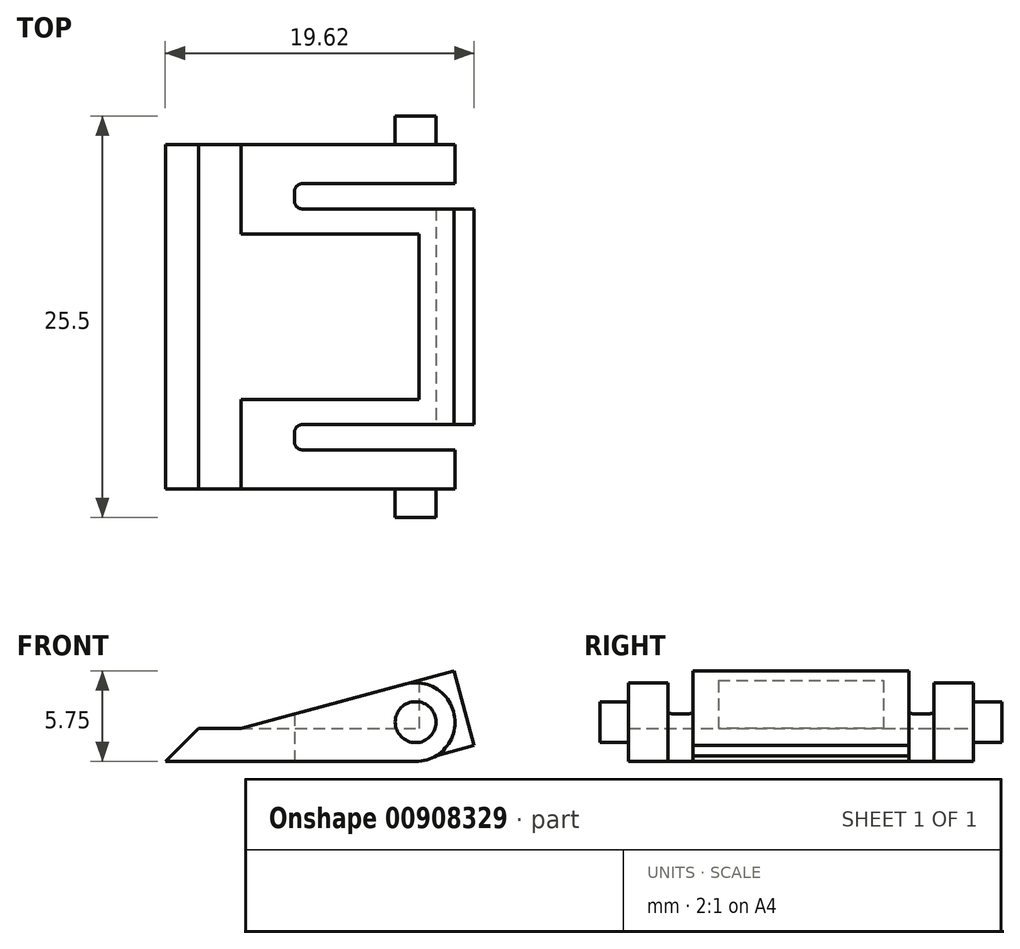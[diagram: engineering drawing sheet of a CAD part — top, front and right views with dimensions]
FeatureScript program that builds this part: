
annotation { "Feature Type Name" : "Feature", "Feature Type Description" : "" }
export const myFeature = defineFeature(function(context is Context, id is Id, definition is map)
    precondition{}
    {
        {
            var Q0;
            Q0=qCreatedBy(makeId("Front.planeOp"),FACE);
            var sketch = newSketch(context, id + "F0", { "sketchPlane" : qUnion([Q0])});
            skLineSegment(sketch, "E0", {"start": v(-10.84, 0) * mm, "end": v(5.06, 0) * mm});
            skArc(sketch, "E1", {"start": v(5.06, 0) * mm, "mid": v(7.54, 2.83) * mm, "end": v(4.41, 4.91) * mm});
            skLineSegment(sketch, "E2", {"start": v(-10.84, 0) * mm, "end": v(-8.74, 2.1) * mm});
            skLineSegment(sketch, "E3", {"start": v(-8.74, 2.1) * mm, "end": v(-6.04, 2.1) * mm});
            skLineSegment(sketch, "E4", {"start": v(-6.04, 2.1) * mm, "end": v(4.41, 4.91) * mm});
            skSolve(sketch);
        }
        {
            var Q0;
            Q0 = qSketchRegion(id + "F0", true);
            extrude(context, id + "F1", {"entities" : qUnion([Q0]), "endBound" : BoundingType.SYMMETRIC, "depth" : 21.9 * mm, "offsetDistance" : 25 * mm});
        }
        {
            var Q0;
            Q0=makeQuery(id+"F1.opExtrude","CAP_FACE",FACE,{"disambiguationData":[OSD([sQuery(id+"F0.wireOp",EDGE,"E0"),sQuery(id+"F0.wireOp",EDGE,"E1"),sQuery(id+"F0.wireOp",EDGE,"E2"),sQuery(id+"F0.wireOp",EDGE,"E3"),sQuery(id+"F0.wireOp",EDGE,"E4")])],"isStart":false});
            var sketch = newSketch(context, id + "F2", { "sketchPlane" : qUnion([Q0])});
            skPoint(sketch, "E5.0", {"position": v(5.06, 2.5) * mm});
            skCircle(sketch, "E6", {"center": v(5.06, 2.5) * mm, "radius": 1.3 * mm});
            skSolve(sketch);
        }
        {
            var Q0;
            Q0 = qSketchRegion(id + "F2", true);
            extrude(context, id + "F3", {"entities" : qUnion([Q0]), "operationType" : NewBodyOperationType.ADD, "depth" : 1.8 * mm, "offsetDistance" : 25 * mm});
        }
        {
            var Q0;
            Q0=makeQuery(id+"F1.opExtrude","SWEPT_BODY",BODY,{"disambiguationData":[OSD([sQuery(id+"F0.wireOp",EDGE,"E0"),sQuery(id+"F0.wireOp",EDGE,"E1"),sQuery(id+"F0.wireOp",EDGE,"E2"),sQuery(id+"F0.wireOp",EDGE,"E3"),sQuery(id+"F0.wireOp",EDGE,"E4")])]});
            var Q1;
            Q1=qCreatedBy(makeId("Front.planeOp"),FACE);
            mirror(context, id + "F4", {"operationType" : NewBodyOperationType.ADD, "entities" : qUnion([Q0]), "mirrorPlane" : qUnion([Q1])});
        }
        {
            var Q0;
            Q0=qCreatedBy(makeId("Top.planeOp"),FACE);
            var sketch = newSketch(context, id + "F5", { "sketchPlane" : qUnion([Q0])});
            skLineSegment(sketch, "E7", {"start": v(-2.14, 8.45) * mm, "end": v(9.36, 8.45) * mm});
            skLineSegment(sketch, "E8", {"start": v(9.36, 8.45) * mm, "end": v(9.36, 6.85) * mm});
            skLineSegment(sketch, "E9", {"start": v(9.36, 6.85) * mm, "end": v(-2.14, 6.85) * mm});
            skLineSegment(sketch, "E10", {"start": v(-2.64, 7.35) * mm, "end": v(-2.64, 7.95) * mm});
            skPoint(sketch, "E11.visualSharp", {"position": v(-2.64, 8.45) * mm});
            skArc(sketch, "E11.filletArc", {"start": v(-2.14, 8.45) * mm, "mid": v(-2.5, 8.3) * mm, "end": v(-2.64, 7.95) * mm});
            skPoint(sketch, "E12.visualSharp", {"position": v(-2.64, 6.85) * mm});
            skArc(sketch, "E12.filletArc", {"start": v(-2.64, 7.35) * mm, "mid": v(-2.5, 7) * mm, "end": v(-2.14, 6.85) * mm});
            skLineSegment(sketch, "E13.MirrorCS", {"start": v(9.36, -6.85) * mm, "end": v(-2.14, -6.85) * mm});
            skLineSegment(sketch, "E14.MirrorCS", {"start": v(9.36, -8.45) * mm, "end": v(9.36, -6.85) * mm});
            skLineSegment(sketch, "E15.MirrorCS", {"start": v(-2.14, -8.45) * mm, "end": v(9.36, -8.45) * mm});
            skArc(sketch, "E16.MirrorCS", {"start": v(-2.14, -8.45) * mm, "mid": v(-2.5, -8.3) * mm, "end": v(-2.64, -7.95) * mm});
            skLineSegment(sketch, "E17.MirrorCS", {"start": v(-2.64, -7.35) * mm, "end": v(-2.64, -7.95) * mm});
            skArc(sketch, "E18.MirrorCS", {"start": v(-2.64, -7.35) * mm, "mid": v(-2.5, -7) * mm, "end": v(-2.14, -6.85) * mm});
            skSolve(sketch);
        }
        {
            var Q0;
            Q0 = qSketchRegion(id + "F5", true);
            extrude(context, id + "F6", {"entities" : qUnion([Q0]), "operationType" : NewBodyOperationType.REMOVE, "endBound" : BoundingType.THROUGH_ALL, "depth" : 25 * mm, "offsetDistance" : 25 * mm});
        }
        {
            var Q0;
            Q0=makeQuery(id+"F6.boolean.opBoolean","COPY",FACE,{"derivedFrom":makeQuery(id+"F6.opExtrude","SWEPT_FACE",FACE,{"disambiguationData":[OSD([sQuery(id+"F5.wireOp",EDGE,"E13.MirrorCS")])]})});
            var sketch = newSketch(context, id + "F7", { "sketchPlane" : qUnion([Q0])});
            skLineSegment(sketch, "E19", {"start": v(4.41, 4.91) * mm, "end": v(7.5, 5.75) * mm});
            skLineSegment(sketch, "E20", {"start": v(7.5, 5.75) * mm, "end": v(8.78, 1.01) * mm});
            skLineSegment(sketch, "E21", {"start": v(8.78, 1.01) * mm, "end": v(6.36, 0.36) * mm});
            skArc(sketch, "E22.0", {"start": v(6.36, 0.36) * mm, "mid": v(7.36, 3.48) * mm, "end": v(4.41, 4.91) * mm});
            skPoint(sketch, "E23.orphan", {"position": v(5.06, 0) * mm});
            skSolve(sketch);
        }
        {
            var Q0;
            Q0=makeQuery(id+"F7.imprint","IMPRINT",FACE,{"disambiguationData":[TD([[makeQuery(id+"F7.imprint","IMPRINT",EDGE,{"derivedFrom":sQuery(id+"F7.wireOp",EDGE,"E19")}),-1.0]])]});
            var Q1;
            Q1=makeQuery(id+"F6.boolean.opBoolean","COPY",FACE,{"derivedFrom":makeQuery(id+"F6.opExtrude","SWEPT_FACE",FACE,{"disambiguationData":[OSD([sQuery(id+"F5.wireOp",EDGE,"E9")])]})});
            extrude(context, id + "F8", {"entities" : qUnion([Q0]), "operationType" : NewBodyOperationType.ADD, "endBound" : BoundingType.UP_TO_SURFACE, "oppositeDirection" : true, "depth" : 25 * mm, "endBoundEntityFace" : qUnion([Q1]), "offsetDistance" : 25 * mm});
        }
        {
            var Q0;
            Q0=makeQuery(id+"F1.opExtrude","SWEPT_FACE",FACE,{"disambiguationData":[OSD([sQuery(id+"F0.wireOp",EDGE,"E3")])]});
            var sketch = newSketch(context, id + "F9", { "sketchPlane" : qUnion([Q0])});
            skLineSegment(sketch, "E24.bottom", {"start": v(-6.04, 5.25) * mm, "end": v(5.26, 5.25) * mm});
            skLineSegment(sketch, "E24.top", {"start": v(-6.04, -5.25) * mm, "end": v(5.26, -5.25) * mm});
            skLineSegment(sketch, "E24.left", {"start": v(-6.04, 5.25) * mm, "end": v(-6.04, -5.25) * mm});
            skLineSegment(sketch, "E24.right", {"start": v(5.26, 5.25) * mm, "end": v(5.26, -5.25) * mm});
            skSolve(sketch);
        }
        {
            var Q0;
            Q0 = qSketchRegion(id + "F9", true);
            extrude(context, id + "F10", {"entities" : qUnion([Q0]), "operationType" : NewBodyOperationType.REMOVE, "endBound" : BoundingType.THROUGH_ALL, "depth" : 25 * mm, "offsetDistance" : 25 * mm});
        }
    });
